# Revit family: Hager-Orion_Plus-IP65-D160-Cl.I-Steel_encl-630A-NoHosted-UK-en
name_source: partatom
category: Electrical Equipment
units: mm (PartAtom-declared; Revit-internal decimal feet)

## family parameters
Always vertical = Yes
Cut with Voids When Loaded = No
Panel Configuration = Two Columns, Circuits Across
Part Type = Panelboard
Room Calculation Point = No
Round Connector Dimension = Use Diameter
Shared = No
Work Plane-Based = Yes

## types (8) — shared parameters
Default Elevation = 1219 mm
EF000003 - Mounting method = EV000384 - Surface mounted (plaster)
EF000007 - Colour = EV000270 - Grey
EF000049 - Depth = 160 mm  [stored 0.524934 ft]
EF000116 - RAL-number = 7035
EF000118 - With mounting plate = No
EF000437 - Number of conduit inlets = 2
EF001131 - Internal depth = 160 mm  [stored 0.524934 ft]
EF001596 - Material housing = EV000179 - Steel
EF001613 - Circuit integrity = EV000494 - None
EF003532 - Suitable for outdoor use = No
EF004293 - Impact strength = EV008784 - IK10
EF004464 - Type of door = EV002646 - Single
EF005474 - Degree of protection (IP) = EV006421 - IP65
EF006306 - With lock = Yes
EF007800 - Suitable for lightning protection = No
EF008873 - Nominal current (In) = 630 A
EF009171 - Material plate thickness door/cover = 2 mm  [stored 0.00656168 ft]
EF015940 - Cover with overpressure release = No
HG000002 - With door or cover = Yes
HG000003 - Range = Orion Plus
HG000006 - Flush mounted = No
HG000009 - Double swing door = No
HG000010 - Asymmetric doors = No
HG000023 - Double section enclosure = No
HG000024 - Bottom section height = 600 mm
HG000026 - Floor standing = No
Manufacturer = Hager
Type Comments = Orion Plus
zero-valued in all types: EF000218 - Built-in depth, HG000027 - Plinth height

## per-type parameters (varying)
| type | EF000008 - Width | EF000040 - Height | EF000266 - Number of rows | EF000339 - Type of cover | EF001088 - Extension possible | EF002950 - Width in number of modular spacings | EF004427 - Number of modules | EF006244 - Transparent cover/door | EF009170 - Material plate thickness cabinet | EF009212 - Cover model | EF009554 - Number of openings for flange plates | HG000004 - Manufacturer reference |
| Surface mounted (plaster) IP65 W200 H250 D160  - FL101A | 200 mm  [stored 0.656168 ft] | 250 mm  [stored 0.82021 ft] | 0 | EV004216 - Door | No | 0 | 0 | No | 2 mm  [stored 0.00656168 ft] | EV009916 - With notch | 0 | FL101A |
| Surface mounted (plaster) IP65 W250 H300 D160  - FL102A | 250 mm  [stored 0.82021 ft] | 300 mm | 1 | EV004216 - Door | Yes | 0 | 0 | No | 2 mm  [stored 0.00656168 ft] | EV009916 - With notch | 2 | FL102A |
| Surface mounted (plaster) IP65 W300 H300 D160  - FL103A | 300 mm | 300 mm | 0 | EV004216 - Door | No | 0 | 0 | No | 2 mm  [stored 0.00656168 ft] | EV009916 - With notch | 0 | FL103A |
| Surface mounted (plaster) IP65 W300 H350 D160  - FL104A | 300 mm | 350 mm  [stored 1.14829 ft] | 2 | EV001012 - Cover | Yes | 10 | 20 | No | 2 mm  [stored 0.00656168 ft] | EV000116 - Closed | 2 | FL104A |
| Surface mounted (plaster) IP65 W300 H350 D160  - FL154A | 300 mm | 350 mm  [stored 1.14829 ft] | 2 | EV004216 - Door | Yes | 10 | 20 | Yes | 1 mm  [stored 0.00328084 ft] | EV000116 - Closed | 2 | FL154A |
| Surface mounted (plaster) IP65 W300 H400 D160  - FL106A | 300 mm | 400 mm  [stored 1.31234 ft] | 0 | EV004216 - Door | No | 0 | 0 | No | 2 mm  [stored 0.00656168 ft] | EV009916 - With notch | 2 | FL106A |
| Surface mounted (plaster) IP65 W300 H500 D160  - FL109A | 300 mm | 500 mm  [stored 1.64042 ft] | 3 | EV004216 - Door | Yes | 10 | 30 | No | 1 mm  [stored 0.00328084 ft] | EV000116 - Closed | 2 | FL109A |
| Surface mounted (plaster) IP65 W400 H500 D160  - FL111A | 400 mm  [stored 1.31234 ft] | 500 mm  [stored 1.64042 ft] | 3 | EV004216 - Door | Yes | 16 | 54 | No | 1 mm  [stored 0.00328084 ft] | EV000116 - Closed | 2 | FL111A |

note: [stored X ft] marks values corroborated as IEEE doubles in the binary element streams (Revit-internal decimal feet)

## geometry (parser evidence)
native form markers: Blend x4, Sweep x11
no freeform markers — native parametric forms only
